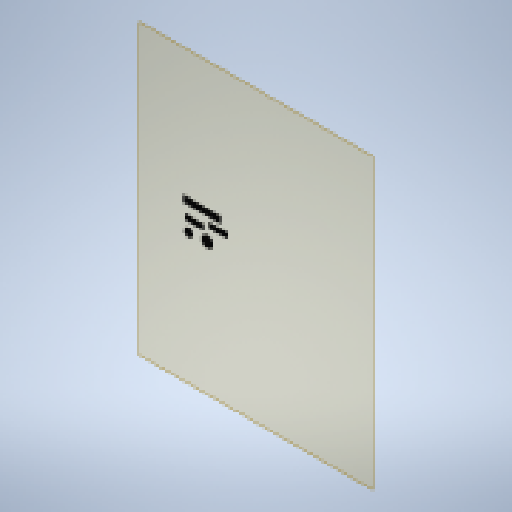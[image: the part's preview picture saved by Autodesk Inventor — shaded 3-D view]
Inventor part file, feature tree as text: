
AUTODESK INVENTOR PART (.ipt)
format: ipt  version: 2023 (Build 270158030, 158C)  size: 190,976 bytes
history: native  units: mm
features: other x5, sketch x2, plane x1, extrude x1
ambient origin geometry x8: Origin, YZ Plane, XZ Plane, XY Plane, X Axis, Y Axis, Z Axis, Center Point
bodies: Solid1 (feature_tree)
feature tree (9):
  plane  "Work Plane1"
  extrude  "Extrusion1"  Depth=12.0mm
  other  "Decal1"
  sketch  "Sketch1"  dims[d0=70.0mm d1=12.0mm]
  sketch  "Sketch2"  dims[d2=16.0mm d3=20.0mm d4=22.0mm d5=29.0mm d6=10.0mm d7=35.0mm d8=10.0mm d9=35.0mm d10=3.0mm d11=8.5mm d12=25.0mm d13=2.5mm d14=35.0mm d15=9.0mm d16=20.0mm d17=15.0mm d18=1.0mm d19=0.0mm]
  other  "Image1"
  other  "<userpath>\Documents\0004-inventor\Inventor_Projects\electronics-enclosure\enclosure.iam"
  other  "enclosure.iam"
  other  "door:1"
